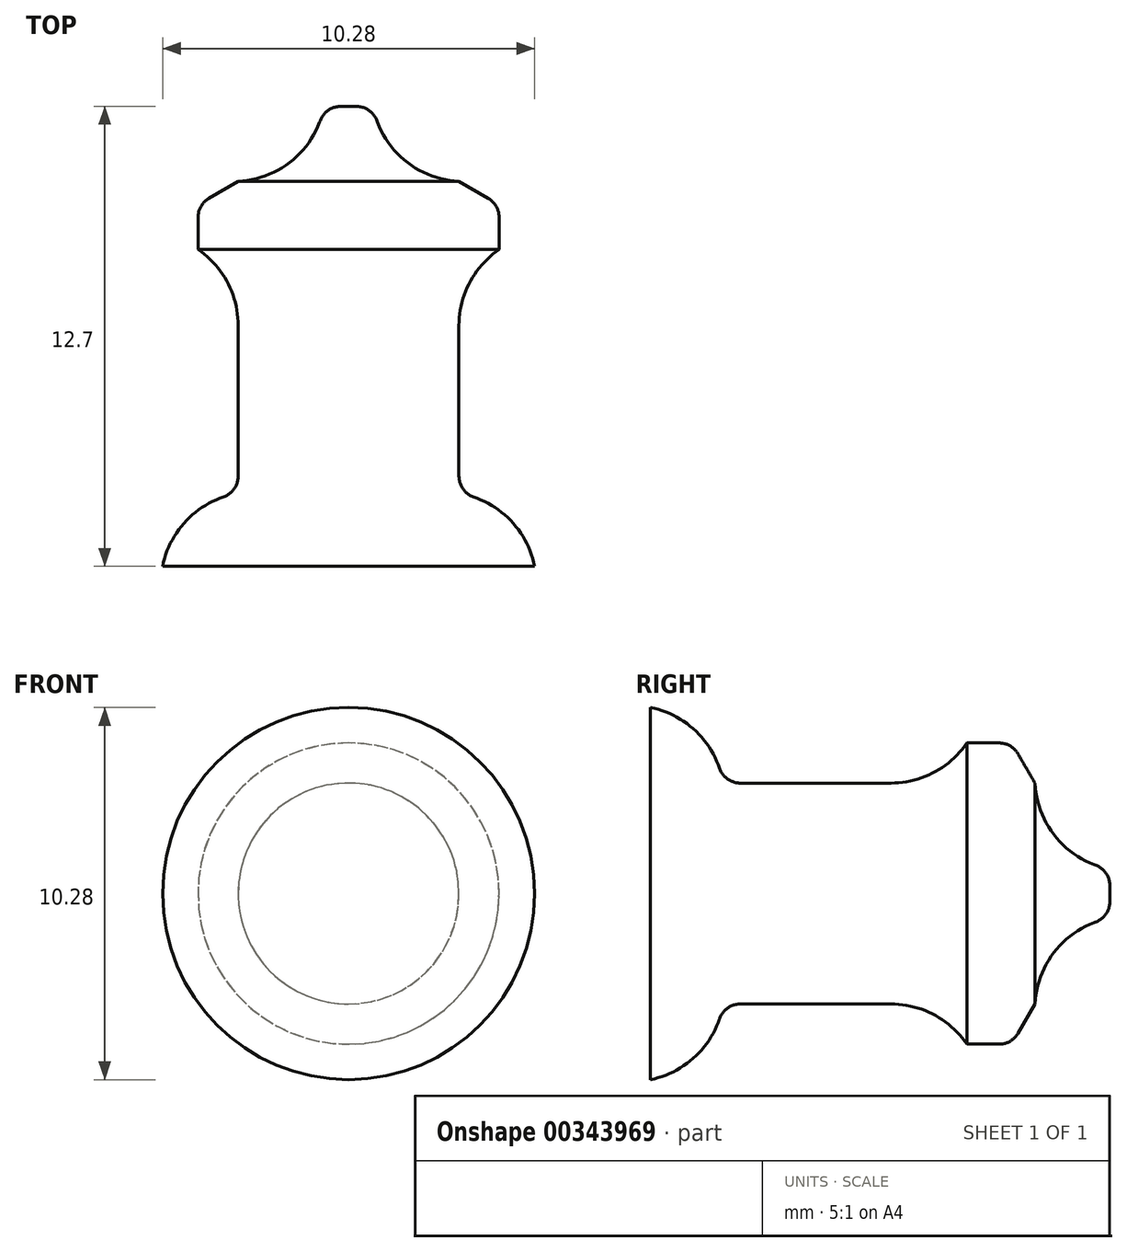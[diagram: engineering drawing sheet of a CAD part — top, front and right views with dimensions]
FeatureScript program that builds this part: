
annotation { "Feature Type Name" : "Feature", "Feature Type Description" : "" }
export const myFeature = defineFeature(function(context is Context, id is Id, definition is map)
    precondition{}
    {
        {
            var Q0;
            Q0=qCreatedBy(makeId("Right.planeOp"),FACE);
            var sketch = newSketch(context, id + "F0", { "sketchPlane" : qUnion([Q0])});
            skLineSegment(sketch, "E0", {"start": v(0, 0) * mm, "end": v(-12.7, 0) * mm});
            skLineSegment(sketch, "E1", {"start": v(-12.7, 0) * mm, "end": v(-12.7, 5.14) * mm});
            skLineSegment(sketch, "E2", {"start": v(-12.7, 5.14) * mm, "end": v(-11.43, 5.14) * mm});
            skLineSegment(sketch, "E3", {"start": v(-11.43, 5.14) * mm, "end": v(-10.63, 3.05) * mm});
            skLineSegment(sketch, "E4", {"start": v(-10.63, 3.05) * mm, "end": v(-4.52, 3.05) * mm});
            skLineSegment(sketch, "E5", {"start": v(-4.52, 3.05) * mm, "end": v(-3.95, 4.16) * mm});
            skLineSegment(sketch, "E6", {"start": v(-3.95, 4.16) * mm, "end": v(-2.71, 4.16) * mm});
            skLineSegment(sketch, "E7", {"start": v(-2.71, 4.16) * mm, "end": v(-2.07, 3.05) * mm});
            skLineSegment(sketch, "E8", {"start": v(-2.07, 3.05) * mm, "end": v(-2.69, 1.66) * mm});
            skLineSegment(sketch, "E9", {"start": v(0, 0.63) * mm, "end": v(-2.69, 1.66) * mm});
            skLineSegment(sketch, "E10", {"start": v(0, 0.64) * mm, "end": v(0, 0) * mm});
            skSolve(sketch);
        }
        {
            var Q0;
            Q0=makeQuery(id+"F0.imprint","IMPRINT",FACE,{"disambiguationData":[TD([[makeQuery(id+"F0.imprint","IMPRINT",EDGE,{"derivedFrom":sQuery(id+"F0.wireOp",EDGE,"E0")}),-1.0]])]});
            var Q1;
            Q1=sQuery(id+"F0.wireOp",EDGE,"E0");
            revolve(context, id + "F1", {"entities" : qUnion([Q0]), "axis" : qUnion([Q1]), "revolveType" : RevolveType.FULL});
        }
        {
            var Q0;
            Q0=makeQuery(id+"F1.opRevolve","SWEPT_EDGE",EDGE,{"disambiguationData":[OSD([sQuery(id+"F0.wireOp",EDGE,"E2"),sQuery(id+"F0.wireOp",EDGE,"E3")])]});
            var Q1;
            Q1=makeQuery(id+"F1.opRevolve","SWEPT_EDGE",EDGE,{"disambiguationData":[OSD([sQuery(id+"F0.wireOp",EDGE,"E4"),sQuery(id+"F0.wireOp",EDGE,"E5")])]});
            var Q2;
            Q2=makeQuery(id+"F1.opRevolve","SWEPT_EDGE",EDGE,{"disambiguationData":[OSD([sQuery(id+"F0.wireOp",EDGE,"E8"),sQuery(id+"F0.wireOp",EDGE,"E9")])]});
            fillet(context, id + "F2", {"entities" : qUnion([Q0, Q1, Q2]), "radius" : 2.54 * mm, "tangentPropagation" : true, "allowEdgeOverflow" : false});
        }
        {
            var Q0;
            Q0=makeQuery(id+"F1.opRevolve","SWEPT_EDGE",EDGE,{"disambiguationData":[OSD([sQuery(id+"F0.wireOp",EDGE,"E3"),sQuery(id+"F0.wireOp",EDGE,"E4")])]});
            var Q1;
            Q1=makeQuery(id+"F1.opRevolve","SWEPT_EDGE",EDGE,{"disambiguationData":[OSD([sQuery(id+"F0.wireOp",EDGE,"E6"),sQuery(id+"F0.wireOp",EDGE,"E7")])]});
            var Q2;
            Q2=makeQuery(id+"F1.opRevolve","SWEPT_EDGE",EDGE,{"disambiguationData":[OSD([sQuery(id+"F0.wireOp",EDGE,"E9"),sQuery(id+"F0.wireOp",EDGE,"E10")])]});
            fillet(context, id + "F3", {"entities" : qUnion([Q0, Q1, Q2]), "radius" : 0.6 * mm, "tangentPropagation" : true, "allowEdgeOverflow" : false});
        }
    });
